# Revit family: Building-ConnessioniIEC309-GEWISS-67IB-PRESE-INTERBLOCCATE_IP67_CON_FONDO_FUS
name_source: partatom
category: Apparecchi elettrici
units: mm (PartAtom-declared; Revit-internal decimal feet)

## family parameters
Condiviso = Sì
Host = Superficie
Mantenere orientamento annotazione = Sì
Punto di calcolo locali = Sì
Quota connettore circolare = Usa diametro
Taglio con vuoti quando caricato = Sì
Tipo di parte = Normale

## types (23) — shared parameters
Catalogo = BUILDING
Catalogo Serie = 67 IB
Codice Electrocod = 2222
Con fondo = Si
Corpo presa = Grigio RAL - 7035
Corrente nominale di cortocircuito (Icc) = 10KA
Frequenza = 50/60 Hz
Frequenza nominale (Hz) = 50/60 Hz
Glow Wire Test = 850 °C (Presa IB) - 650 °C (Cassetta di fondo)
Glow wire test: = 850 °C (Presa IB) - 650 °C (Cassetta di fondo)
Grado di protezione = IP67
IDF = f60054a8-4916-4fde-b3af-4822cbe090e7
IDT = 3a2f285e-e7b7-489c-a67e-4c14f132aefb
Immagine tipo = I.jpg
Potere di interruzione fusibili = > 50 kA
Produttore = GEWISS S.p.A.
Prospetto di default = 1219 mm
Protezione = Base portafusibile (CBF)
Resistenza agli urti = IK08
SEO = Presa
Scheda Tecnica = https://www.gewiss.com
Simbolo presa = PRESAINDSTAGNA : 3P
Struttura = Grigio RAL - 7035
Temperatura di funzionamento = -25 ÷ +40 °C
Temperatura di utilizzo = -25 +40 °C
Tensione nominale di isolamento (Ui) = 500V
Tensione nominale di tenuta ad impulso = 4KV
Termopressione con biglia = 125 °C (Presa IB) - 80 °C (Cassetta di fondo)
Tipo fusibile = Ã˜ 10,3x38 mm
Tipologia = Verticale
URL = https://www.gewiss.com
Versione file RFA = 21.4
presa = Grigio RAL - 7035
zero-valued in all types: giallo

## per-type parameters (varying)
| type | Codice EAN | Colore | Colore: | Corrente nominale (A) | Corrente nominale (In) | Corrente nominale (In) presa IB | Descrizione | Modello | N. poli | Numero di poli | Peso | Peso (kg) | Riferimento h | Tensione nominale | Tensione nominale: |
| GW66225N - PR.BL IP67 C.F.3P+N+T 16A 110V 4H CBF | 8011564741355 | Giallo | Giallo | 16 | 16 | 16A | PR.BL IP67 C.F.3P+N+T 16A 110V 4H CBF | GW66225N | 3P+N+T | 3P+N+T | Max. 1,0 Kg | Max. 1,0 Kg | 4 | 100 - 130 V | 100 - 130 V |
| GW66226N - PR.BL IP67 C.F.2P+T 16A 230V 6H CBF | 8011564741362 | Blu | Blu | 16 | 16 | 16A | PR.BL IP67 C.F.2P+T 16A 230V 6H CBF | GW66226N | 2P+T | 2P+T | Max. 1,0 Kg | Max. 1,0 Kg | 6 | 200 - 250 V | 200 - 250 V |
| GW66242N - PR.BL IP67 C.F.3P+N+T 32A 400V 6H CBF | 8011564742567 | Rosso | Rosso | 32 | 32 | 28A | PR.BL IP67 C.F.3P+N+T 32A 400V 6H CBF | GW66242N | 3P+N+T | 3P+N+T | Max. 1,1 Kg | Max. 1,1 Kg | 6 | 380 - 415 V | 380 - 415 V |
| GW66258N - PR.BL IP67 C.F.3P+T 32A 380V 3H CBF | 8011564741539 | Rosso | Rosso | 32 | 32 | 28A | PR.BL IP67 C.F.3P+T 32A 380V 3H CBF | GW66258N | 3P+T | 3P+T | Max. 1,1 Kg | Max. 1,1 Kg | 3 | 380 - 440 V | 380 - 440 V |
| GW66231N - PR.BL IP67 C.F.3P+N+T 16A 400V 6H CBF | 8011564742543 | Rosso | Rosso | 16 | 16 | 16A | PR.BL IP67 C.F.3P+N+T 16A 400V 6H CBF | GW66231N | 3P+N+T | 3P+N+T | Max. 1,0 Kg | Max. 1,0 Kg | 6 | 380 - 415 V | 380 - 415 V |
| GW66240N - PR.BL IP67 C.F.2P+T 32A 400V 9H CBF | 8011564741485 | Rosso | Rosso | 32 | 32 | 32A | PR.BL IP67 C.F.2P+T 32A 400V 9H CBF | GW66240N | 2P+T | 2P+T | Max. 1,1 Kg | Max. 1,1 Kg | 9 | 380 - 415 V | 380 - 415 V |
| GW66227N - PR.BL IP67 C.F.3P+T 16A 230V 9H CBF | 8011564741379 | Blu | Blu | 16 | 16 | 16A | PR.BL IP67 C.F.3P+T 16A 230V 9H CBF | GW66227N | 3P+T | 3P+T | Max. 1,0 Kg | Max. 1,0 Kg | 9 | 200 - 250 V | 200 - 250 V |
| GW66236N - PR.BL IP67 C.F.3P+N+T 32A 110V 4H CBF | 8011564741454 | Giallo | Giallo | 32 | 32 | 28A | PR.BL IP67 C.F.3P+N+T 32A 110V 4H CBF | GW66236N | 3P+N+T | 3P+N+T | Max. 1,1 Kg | Max. 1,1 Kg | 4 | 100 - 130 V | 100 - 130 V |
| GW66223N - PR.BL IP67 C.F.2P+T 16A 110V 4H CBF | 8011564741331 | Giallo | Giallo | 16 | 16 | 16A | PR.BL IP67 C.F.2P+T 16A 110V 4H CBF | GW66223N | 2P+T | 2P+T | Max. 1,0 Kg | Max. 1,0 Kg | 4 | 100 - 130 V | 100 - 130 V |
| GW66241N - PR.BL IP67 C.F.3P+T 32A 400V 6H CBF | 8011564741492 | Rosso | Rosso | 32 | 32 | 28A | PR.BL IP67 C.F.3P+T 32A 400V 6H CBF | GW66241N | 3P+T | 3P+T | Max. 1,1 Kg | Max. 1,1 Kg | 6 | 380 - 415 V | 380 - 415 V |
| GW66235N - PR.BL IP67 C.F.3P+T 32A 110V 4H CBF | 8011564741447 | Giallo | Giallo | 32 | 32 | 28A | PR.BL IP67 C.F.3P+T 32A 110V 4H CBF | GW66235N | 3P+T | 3P+T | Max. 1,1 Kg | Max. 1,1 Kg | 4 | 100 - 130 V | 100 - 130 V |
| GW66234N - PR.BL IP67 C.F.2P+T 32A 110V 4H CBF | 8011564741430 | Giallo | Giallo | 32 | 32 | 32A | PR.BL IP67 C.F.2P+T 32A 110V 4H CBF | GW66234N | 2P+T | 2P+T | Max. 1,1 Kg | Max. 1,1 Kg | 4 | 100 - 130 V | 100 - 130 V |
| GW66243N - PR.BL IP67 C.F.3P+T 32A 500V 7H CBF | 8011564741508 | Nero | Nero | 32 | 32 | 28A | PR.BL IP67 C.F.3P+T 32A 500V 7H CBF | GW66243N | 3P+T | 3P+T | Max. 1,1 Kg | Max. 1,1 Kg | 7 | 480 - 500 V | 480 - 500 V |
| GW66233N - PR.BL IP67 C.F.3P+N+T 16A 500V 7H CBF | 8011564741423 | Nero | Nero | 16 | 16 | 16A | PR.BL IP67 C.F.3P+N+T 16A 500V 7H CBF | GW66233N | 3P+N+T | 3P+N+T | Max. 1,0 Kg | Max. 1,0 Kg | 7 | 480 - 500 V | 480 - 500 V |
| GW66228N - PR.BL IP67 C.F.3P+N+T 16A 230V 9H CBF | 8011564741386 | Blu | Blu | 16 | 16 | 16A | PR.BL IP67 C.F.3P+N+T 16A 230V 9H CBF | GW66228N | 3P+N+T | 3P+N+T | Max. 1,0 Kg | Max. 1,0 Kg | 9 | 200 - 250 V | 200 - 250 V |
| GW66238N - PR.BL IP67 C.F.3P+T 32A 230V 9H CBF | 8011564741461 | Blu | Blu | 32 | 32 | 28A | PR.BL IP67 C.F.3P+T 32A 230V 9H CBF | GW66238N | 3P+T | 3P+T | Max. 1,1 Kg | Max. 1,1 Kg | 9 | 200 - 250 V | 200 - 250 V |
| GW66229N - PR.BL IP67 C.F.2P+T 16A 400V 9H CBF | 8011564741393 | Rosso | Rosso | 16 | 16 | 16A | PR.BL IP67 C.F.2P+T 16A 400V 9H CBF | GW66229N | 2P+T | 2P+T | Max. 1,0 Kg | Max. 1,0 Kg | 9 | 380 - 415 V | 380 - 415 V |
| GW66224N - PR.BL IP67 C.F.3P+T 16A 110V 4H CBF | 8011564741348 | Giallo | Giallo | 16 | 16 | 16A | PR.BL IP67 C.F.3P+T 16A 110V 4H CBF | GW66224N | 3P+T | 3P+T | Max. 1,0 Kg | Max. 1,0 Kg | 4 | 100 - 130 V | 100 - 130 V |
| GW66232N - PR.BL IP67 C.F.3P+T 16A 500V 7H CBF | 8011564741416 | Nero | Nero | 16 | 16 | 16A | PR.BL IP67 C.F.3P+T 16A 500V 7H CBF | GW66232N | 3P+T | 3P+T | Max. 1,0 Kg | Max. 1,0 Kg | 7 | 480 - 500 V | 480 - 500 V |
| GW66237N - PR.BL IP67 C.F.2P+T 32A 230V 6H CBF | 8011564742550 | Blu | Blu | 32 | 32 | 32A | PR.BL IP67 C.F.2P+T 32A 230V 6H CBF | GW66237N | 2P+T | 2P+T | Max. 1,1 Kg | Max. 1,1 Kg | 6 | 200 - 250 V | 200 - 250 V |
| GW66244N - PR.BL IP67 C.F.3P+N+T 32A 500V 7H CBF | 8011564741515 | Nero | Nero | 32 | 32 | 28A | PR.BL IP67 C.F.3P+N+T 32A 500V 7H CBF | GW66244N | 3P+N+T | 3P+N+T | Max. 1,1 Kg | Max. 1,1 Kg | 7 | 480 - 500 V | 480 - 500 V |
| GW66230N - PR.BL IP67 C.F.3P+T 16A 400V 6H CBF | 8011564741409 | Rosso | Rosso | 16 | 16 | 16A | PR.BL IP67 C.F.3P+T 16A 400V 6H CBF | GW66230N | 3P+T | 3P+T | Max. 1,0 Kg | Max. 1,0 Kg | 6 | 380 - 415 V | 380 - 415 V |
| GW66239N - PR.BL IP67 C.F.3P+N+T 32A 230V 9H CBF | 8011564741478 | Blu | Blu | 32 | 32 | 28A | PR.BL IP67 C.F.3P+N+T 32A 230V 9H CBF | GW66239N | 3P+N+T | 3P+N+T | Max. 1,1 Kg | Max. 1,1 Kg | 9 | 200 - 250 V | 200 - 250 V |

## geometry (parser evidence)
native form markers: Sweep x3
no freeform markers — native parametric forms only
